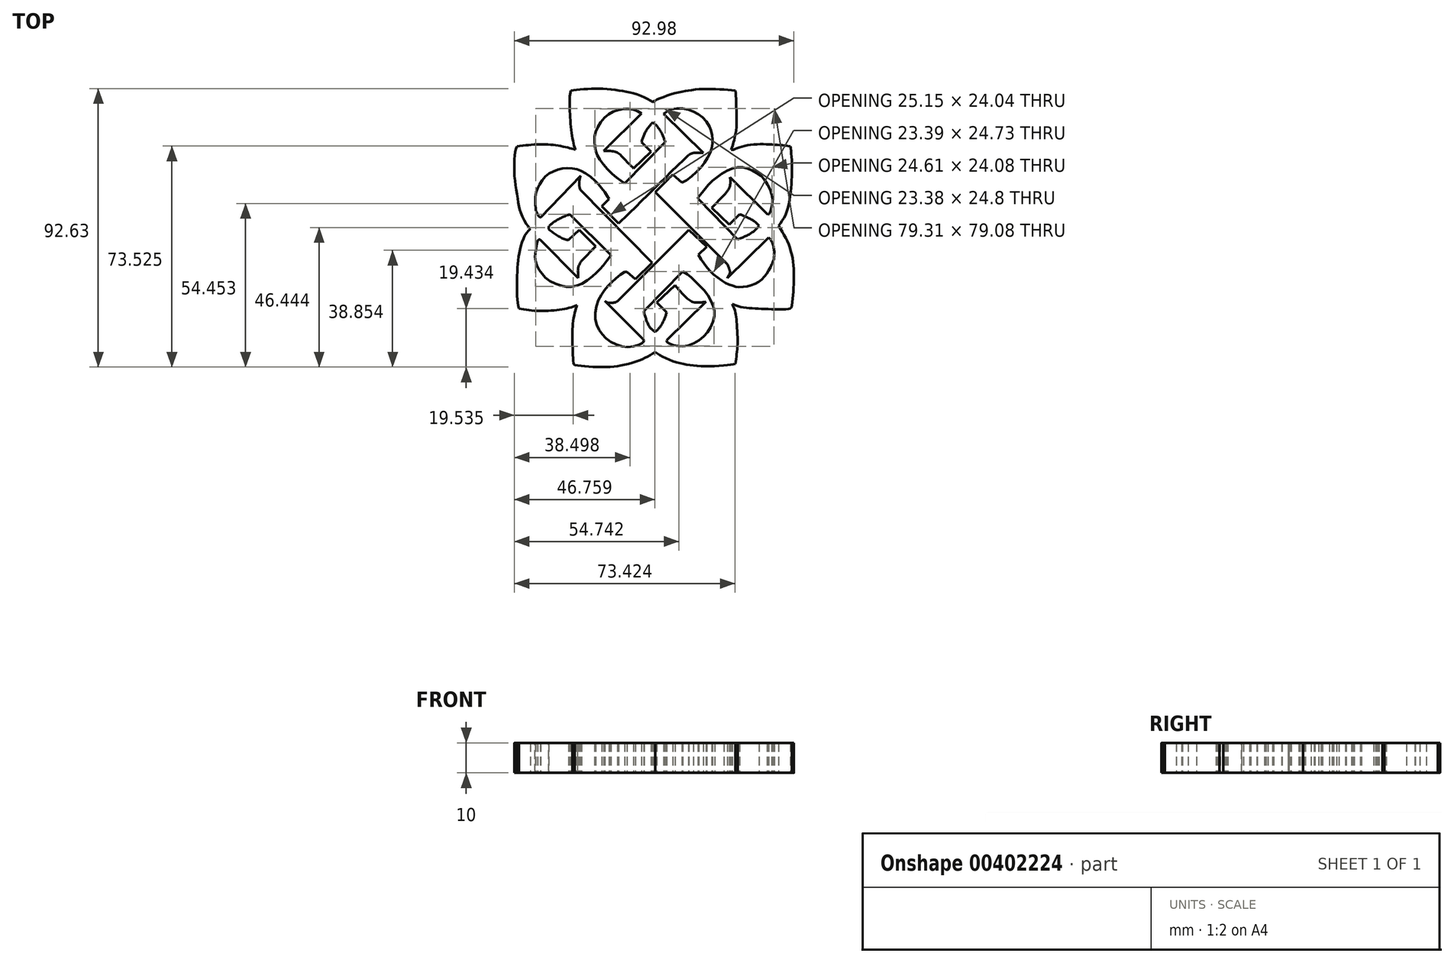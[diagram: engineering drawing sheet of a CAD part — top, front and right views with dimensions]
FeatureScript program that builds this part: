
annotation { "Feature Type Name" : "Feature", "Feature Type Description" : "" }
export const myFeature = defineFeature(function(context is Context, id is Id, definition is map)
    precondition{}
    {
        {
            var Q0;
            Q0=qCreatedBy(makeId("Top.planeOp"),FACE);
            var sketch = newSketch(context, id + "F0", { "sketchPlane" : qUnion([Q0])});
            skFitSpline(sketch, "E0", {"points": [v(25.14, 49.04) * mm, v(30.65, 43.55) * mm], "startDerivative": vector(5.5, -5.49) * mm, "endDerivative": vector(5.5, -5.49) * mm});
            skFitSpline(sketch, "E1", {"points": [v(30.65, 43.55) * mm, v(26, 38.8) * mm], "startDerivative": vector(-4.66, -4.75) * mm, "endDerivative": vector(-4.66, -4.75) * mm});
            skFitSpline(sketch, "E2", {"points": [v(26, 38.8) * mm, v(25.36, 37.84) * mm, v(24.84, 36.64) * mm, v(24.73, 35.05) * mm, v(24.82, 33.01) * mm], "startDerivative": vector(-2.93, -4.28) * mm, "endDerivative": vector(0.35, -7.16) * mm});
            skFitSpline(sketch, "E3", {"points": [v(24.82, 33.01) * mm, v(12.18, 45.71) * mm], "startDerivative": vector(-12.63, 12.7) * mm, "endDerivative": vector(-12.63, 12.7) * mm});
            skFitSpline(sketch, "E4", {"points": [v(12.18, 45.71) * mm, v(11.87, 45.87) * mm, v(11.4, 45.54) * mm], "startDerivative": vector(-0.7, 0.56) * mm, "endDerivative": vector(-0.88, -0.85) * mm});
            skFitSpline(sketch, "E5", {"points": [v(11.4, 45.54) * mm, v(11.08, 44.46) * mm, v(10.68, 42.28) * mm, v(10.47, 40.66) * mm, v(10.64, 38.94) * mm, v(11.02, 37.26) * mm, v(12.18, 35.32) * mm, v(13.55, 33.61) * mm, v(15.9, 31.77) * mm, v(19.27, 30.43) * mm, v(21.46, 30.1) * mm, v(24.16, 30.49) * mm, v(27.14, 31.79) * mm, v(30, 34.01) * mm, v(31.82, 35.74) * mm, v(33.53, 37.63) * mm, v(35.58, 40.39) * mm], "startDerivative": vector(-7.4, -22.6) * mm, "endDerivative": vector(27.9, 39.07) * mm});
            skFitSpline(sketch, "E6", {"points": [v(35.58, 40.39) * mm, v(35.7, 40.73) * mm], "startDerivative": vector(0.11, 0.34) * mm, "endDerivative": vector(0.11, 0.34) * mm});
            skFitSpline(sketch, "E7", {"points": [v(35.7, 40.73) * mm, v(22.01, 54.3) * mm], "startDerivative": vector(-13.68, 13.56) * mm, "endDerivative": vector(-13.68, 13.56) * mm});
            skFitSpline(sketch, "E8", {"points": [v(22.01, 54.3) * mm, v(20.72, 53.8) * mm, v(18.89, 52.95) * mm, v(16.98, 51.84) * mm, v(15.66, 50.83) * mm, v(15.02, 50.13) * mm], "startDerivative": vector(-6.7, -2.48) * mm, "endDerivative": vector(-3.68, -4.51) * mm});
            skFitSpline(sketch, "E9", {"points": [v(15.02, 50.13) * mm, v(15.02, 49.37) * mm, v(16, 48.49) * mm, v(17.72, 47.27) * mm, v(19.6, 46.26) * mm, v(21.13, 45.71) * mm, v(21.66, 45.71) * mm], "startDerivative": vector(-1.24, -6.24) * mm, "endDerivative": vector(4.43, 0.52) * mm});
            skFitSpline(sketch, "E10", {"points": [v(21.66, 45.71) * mm, v(25.14, 49.04) * mm], "startDerivative": vector(3.48, 3.33) * mm, "endDerivative": vector(3.48, 3.33) * mm});
            skFitSpline(sketch, "E11", {"points": [v(12.31, 53.22) * mm, v(11.64, 53.66) * mm, v(11.22, 54.54) * mm, v(10.7, 55.71) * mm], "startDerivative": vector(-2.5, 1.24) * mm, "endDerivative": vector(-1.5, 3.16) * mm});
            skFitSpline(sketch, "E12", {"points": [v(10.7, 55.71) * mm, v(10.7, 60.78) * mm, v(11.4, 63) * mm, v(12.81, 65.5) * mm, v(14.78, 67.61) * mm, v(17.68, 68.96) * mm, v(20.37, 69.6) * mm, v(23.64, 69.38) * mm, v(25.96, 68.59) * mm, v(29.66, 66.11) * mm, v(31.96, 63.76) * mm, v(34.08, 61.07) * mm, v(35.11, 59.3) * mm], "startDerivative": vector(-2.5, 53.11) * mm, "endDerivative": vector(13.02, -25.08) * mm});
            skFitSpline(sketch, "E13", {"points": [v(35.11, 59.3) * mm, v(32.7, 56.92) * mm], "startDerivative": vector(-2.41, -2.37) * mm, "endDerivative": vector(-2.41, -2.37) * mm});
            skFitSpline(sketch, "E14", {"points": [v(32.7, 56.92) * mm, v(38.27, 51.23) * mm], "startDerivative": vector(5.57, -5.69) * mm, "endDerivative": vector(5.57, -5.69) * mm});
            skFitSpline(sketch, "E15", {"points": [v(38.27, 51.23) * mm, v(61.5, 73.93) * mm], "startDerivative": vector(24.3, 23.14) * mm, "endDerivative": vector(24.3, 23.14) * mm});
            skFitSpline(sketch, "E16", {"points": [v(61.5, 73.93) * mm, v(62.34, 74.43) * mm, v(63.17, 74.69) * mm], "startDerivative": vector(1.64, 1.06) * mm, "endDerivative": vector(1.73, 0.44) * mm});
            skFitSpline(sketch, "E17", {"points": [v(63.17, 74.69) * mm, v(66.49, 74.69) * mm], "startDerivative": vector(3.32, 0) * mm, "endDerivative": vector(3.32, 0) * mm});
            skFitSpline(sketch, "E18", {"points": [v(66.49, 74.69) * mm, v(53.29, 87.73) * mm], "startDerivative": vector(-13.2, 13.04) * mm, "endDerivative": vector(-13.2, 13.04) * mm});
            skFitSpline(sketch, "E19", {"points": [v(53.29, 87.73) * mm, v(54.47, 88.62) * mm, v(55.94, 89.26) * mm, v(58.34, 89.41) * mm, v(60.98, 89.22) * mm, v(63.17, 88.39) * mm, v(65.18, 87.28) * mm, v(66.84, 85.95) * mm, v(68.4, 83.69) * mm, v(68.97, 82.34) * mm, v(69.43, 80.48) * mm, v(69.49, 79.36) * mm, v(69.49, 78.04) * mm, v(69.3, 76.26) * mm, v(68.62, 74.49) * mm, v(67.25, 72.07) * mm, v(66.09, 70.37) * mm, v(63.7, 67.91) * mm, v(61.06, 65.73) * mm, v(59.36, 64.86) * mm], "startDerivative": vector(25.95, 21.12) * mm, "endDerivative": vector(-32.62, -14.19) * mm});
            skFitSpline(sketch, "E20", {"points": [v(59.36, 64.86) * mm, v(56.29, 67.53) * mm], "startDerivative": vector(-3.07, 2.67) * mm, "endDerivative": vector(-3.07, 2.67) * mm});
            skFitSpline(sketch, "E21", {"points": [v(56.29, 67.53) * mm, v(50.5, 61.67) * mm], "startDerivative": vector(-5.59, -5.68) * mm, "endDerivative": vector(-5.59, -5.68) * mm});
            skFitSpline(sketch, "E22", {"points": [v(50.5, 61.67) * mm, v(74.45, 37.61) * mm], "startDerivative": vector(23.95, -24.05) * mm, "endDerivative": vector(23.95, -24.05) * mm});
            skFitSpline(sketch, "E23", {"points": [v(74.45, 37.61) * mm, v(74.95, 36.44) * mm, v(75.25, 35.48) * mm, v(75.24, 34.6) * mm, v(74.69, 33.49) * mm, v(74.45, 33.05) * mm], "startDerivative": vector(2.3, -5.17) * mm, "endDerivative": vector(-1.4, -2.62) * mm});
            skFitSpline(sketch, "E24", {"points": [v(74.45, 33.05) * mm, v(87.78, 46.14) * mm], "startDerivative": vector(13.34, 13.08) * mm, "endDerivative": vector(13.34, 13.08) * mm});
            skFitSpline(sketch, "E25", {"points": [v(87.78, 46.14) * mm, v(88.2, 46.52) * mm], "startDerivative": vector(0.41, 0.38) * mm, "endDerivative": vector(0.41, 0.38) * mm});
            skFitSpline(sketch, "E26", {"points": [v(88.2, 46.52) * mm, v(89.14, 45.28) * mm, v(89.63, 43.97) * mm, v(89.97, 42.62) * mm, v(90, 41.19) * mm, v(89.98, 39.58) * mm, v(89.77, 38.8) * mm, v(89.16, 37.61) * mm], "startDerivative": vector(6.84, -7.84) * mm, "endDerivative": vector(-5.3, -9.98) * mm});
            skFitSpline(sketch, "E27", {"points": [v(89.16, 37.61) * mm, v(88.64, 36.4) * mm, v(87.78, 34.91) * mm, v(86.72, 33.48) * mm, v(85.38, 32.15) * mm, v(83.67, 31.12) * mm, v(81.57, 30.46) * mm, v(79.56, 30.08) * mm, v(77.52, 30.08) * mm, v(76.76, 30.4) * mm, v(74.89, 30.9) * mm, v(73.26, 31.77) * mm, v(70.76, 33.48) * mm, v(68.58, 35.56) * mm, v(66.6, 37.9) * mm, v(64.8, 40.78) * mm], "startDerivative": vector(-8.82, -22.5) * mm, "endDerivative": vector(-20.37, 34.98) * mm});
            skFitSpline(sketch, "E28", {"points": [v(64.8, 40.78) * mm, v(67.6, 43.41) * mm], "startDerivative": vector(2.8, 2.63) * mm, "endDerivative": vector(2.8, 2.63) * mm});
            skFitSpline(sketch, "E29", {"points": [v(67.6, 43.41) * mm, v(61.64, 49.1) * mm], "startDerivative": vector(-5.95, 5.69) * mm, "endDerivative": vector(-5.95, 5.69) * mm});
            skFitSpline(sketch, "E30", {"points": [v(61.64, 49.1) * mm, v(37.82, 25.36) * mm], "startDerivative": vector(-23.82, -23.74) * mm, "endDerivative": vector(-23.82, -23.74) * mm});
            skFitSpline(sketch, "E31", {"points": [v(37.82, 25.36) * mm, v(37.15, 24.97) * mm, v(35.4, 24.78) * mm, v(34.37, 24.97) * mm, v(33.48, 25.62) * mm], "startDerivative": vector(-2.6, -2.09) * mm, "endDerivative": vector(-2.88, 3.27) * mm});
            skFitSpline(sketch, "E32", {"points": [v(33.48, 25.62) * mm, v(46.7, 12.3) * mm], "startDerivative": vector(13.23, -13.31) * mm, "endDerivative": vector(13.23, -13.31) * mm});
            skFitSpline(sketch, "E33", {"points": [v(46.7, 12.3) * mm, v(46.12, 11.42) * mm, v(43.3, 10.3) * mm, v(39.34, 10.32) * mm, v(34.88, 12.3) * mm, v(32.37, 15) * mm, v(30.74, 18.2) * mm, v(30.78, 23.4) * mm, v(32.72, 27.8) * mm, v(34.97, 30.76) * mm, v(37.93, 33.45) * mm, v(40.5, 35.17) * mm, v(41.01, 35.13) * mm], "startDerivative": vector(-8.2, -18.96) * mm, "endDerivative": vector(12.87, -4.69) * mm});
            skFitSpline(sketch, "E34", {"points": [v(41.01, 35.13) * mm, v(43.8, 32.67) * mm], "startDerivative": vector(2.78, -2.46) * mm, "endDerivative": vector(2.78, -2.46) * mm});
            skFitSpline(sketch, "E35", {"points": [v(43.8, 32.67) * mm, v(49.4, 38.11) * mm], "startDerivative": vector(5.6, 5.45) * mm, "endDerivative": vector(5.6, 5.45) * mm});
            skFitSpline(sketch, "E36", {"points": [v(49.4, 38.11) * mm, v(25.55, 62.46) * mm], "startDerivative": vector(-23.85, 24.34) * mm, "endDerivative": vector(-23.85, 24.34) * mm});
            skFitSpline(sketch, "E37", {"points": [v(25.55, 62.46) * mm, v(25.17, 63.93) * mm, v(25.32, 65.98) * mm, v(25.62, 67.08) * mm], "startDerivative": vector(-1.47, 4.14) * mm, "endDerivative": vector(1.1, 3.45) * mm});
            skFitSpline(sketch, "E38", {"points": [v(25.62, 67.08) * mm, v(12.31, 53.22) * mm], "startDerivative": vector(-13.31, -13.87) * mm, "endDerivative": vector(-13.31, -13.87) * mm});
            skFitSpline(sketch, "E39", {"points": [v(49.7, 84.86) * mm, v(51.82, 82.58) * mm, v(53.18, 79.87) * mm, v(53.78, 78.24) * mm], "startDerivative": vector(6.22, -5.76) * mm, "endDerivative": vector(1.94, -5.54) * mm});
            skFitSpline(sketch, "E40", {"points": [v(53.78, 78.24) * mm, v(40.32, 64.55) * mm], "startDerivative": vector(-13.46, -13.7) * mm, "endDerivative": vector(-13.46, -13.7) * mm});
            skFitSpline(sketch, "E41", {"points": [v(40.32, 64.55) * mm, v(37.26, 66.71) * mm, v(33.13, 70.93) * mm, v(30.85, 74.68) * mm, v(30.27, 77.58) * mm, v(30.5, 81.1) * mm, v(32.35, 84.96) * mm, v(35.56, 87.94) * mm, v(39.5, 89.25) * mm, v(43.26, 89.1) * mm, v(45.85, 87.78) * mm], "startDerivative": vector(-30.25, 19.46) * mm, "endDerivative": vector(28.26, -18.1) * mm});
            skFitSpline(sketch, "E42", {"points": [v(45.85, 87.78) * mm, v(33.35, 75.33) * mm], "startDerivative": vector(-12.5, -12.46) * mm, "endDerivative": vector(-12.5, -12.46) * mm});
            skFitSpline(sketch, "E43", {"points": [v(33.35, 75.33) * mm, v(36.47, 75.22) * mm, v(38.43, 74.4) * mm, v(40.32, 72.48) * mm, v(43.24, 69.52) * mm], "startDerivative": vector(12.9, 0.35) * mm, "endDerivative": vector(10.5, -10.32) * mm});
            skFitSpline(sketch, "E44", {"points": [v(43.24, 69.52) * mm, v(49.02, 75.08) * mm], "startDerivative": vector(5.79, 5.56) * mm, "endDerivative": vector(5.79, 5.56) * mm});
            skFitSpline(sketch, "E45", {"points": [v(49.02, 75.08) * mm, v(45.85, 78.24) * mm], "startDerivative": vector(-3.18, 3.16) * mm, "endDerivative": vector(-3.18, 3.16) * mm});
            skFitSpline(sketch, "E46", {"points": [v(45.85, 78.24) * mm, v(46.46, 80.06) * mm, v(47.62, 82.38) * mm, v(49.29, 84.45) * mm, v(49.7, 84.86) * mm], "startDerivative": vector(2.19, 6.94) * mm, "endDerivative": vector(2.42, 2.27) * mm});
            skFitSpline(sketch, "E47", {"points": [v(84.95, 50.48) * mm, v(83.34, 48.7) * mm, v(80.36, 46.93) * mm, v(77.84, 45.83) * mm], "startDerivative": vector(-4.56, -5.96) * mm, "endDerivative": vector(-7.4, -3.04) * mm});
            skFitSpline(sketch, "E48", {"points": [v(77.84, 45.83) * mm, v(64.9, 59.25) * mm], "startDerivative": vector(-12.94, 13.42) * mm, "endDerivative": vector(-12.94, 13.42) * mm});
            skFitSpline(sketch, "E49", {"points": [v(64.9, 59.25) * mm, v(64.77, 59.46) * mm, v(64.71, 59.66) * mm, v(64.74, 59.89) * mm, v(64.9, 60.1) * mm], "startDerivative": vector(-0.57, 0.8) * mm, "endDerivative": vector(0.72, 0.77) * mm});
            skFitSpline(sketch, "E50", {"points": [v(64.9, 60.1) * mm, v(68.82, 64.78) * mm, v(71.62, 67.09) * mm, v(75.13, 69.2) * mm, v(78.44, 69.92) * mm, v(80.85, 69.56) * mm, v(83.84, 68.26) * mm, v(86.15, 66.52) * mm, v(88.12, 63.62) * mm, v(89.28, 60.67) * mm, v(89.47, 58.54) * mm, v(89.24, 56.76) * mm, v(88.55, 54.64) * mm, v(88.04, 54.13) * mm, v(87.7, 54.4) * mm], "startDerivative": vector(37.33, 47.72) * mm, "endDerivative": vector(-11.48, 13.7) * mm});
            skFitSpline(sketch, "E51", {"points": [v(87.7, 54.4) * mm, v(75.38, 66.6) * mm], "startDerivative": vector(-12.31, 12.2) * mm, "endDerivative": vector(-12.31, 12.2) * mm});
            skFitSpline(sketch, "E52", {"points": [v(75.38, 66.6) * mm, v(75.38, 64.05) * mm, v(74.9, 62.62) * mm, v(73.35, 60.68) * mm], "startDerivative": vector(0.33, -7.61) * mm, "endDerivative": vector(-5.02, -5.62) * mm});
            skFitSpline(sketch, "E53", {"points": [v(73.35, 60.68) * mm, v(69.22, 56.49) * mm], "startDerivative": vector(-4.13, -4.2) * mm, "endDerivative": vector(-4.13, -4.2) * mm});
            skFitSpline(sketch, "E54", {"points": [v(69.22, 56.49) * mm, v(75.04, 50.86) * mm], "startDerivative": vector(5.82, -5.62) * mm, "endDerivative": vector(5.82, -5.62) * mm});
            skFitSpline(sketch, "E55", {"points": [v(75.04, 50.86) * mm, v(78.52, 54.27) * mm], "startDerivative": vector(3.48, 3.41) * mm, "endDerivative": vector(3.48, 3.41) * mm});
            skFitSpline(sketch, "E56", {"points": [v(78.52, 54.27) * mm, v(80.36, 53.53) * mm, v(83.34, 51.97) * mm, v(84.95, 50.48) * mm], "startDerivative": vector(5.65, -2.18) * mm, "endDerivative": vector(4.43, -4.8) * mm});
            skFitSpline(sketch, "E57", {"points": [v(50.4, 15.13) * mm, v(48.72, 16.62) * mm, v(47.45, 19.22) * mm, v(46.63, 21.95) * mm], "startDerivative": vector(-5.89, 4.24) * mm, "endDerivative": vector(-2.14, 7.84) * mm});
            skFitSpline(sketch, "E58", {"points": [v(46.63, 21.95) * mm, v(59.62, 35.22) * mm], "startDerivative": vector(12.99, 13.27) * mm, "endDerivative": vector(12.99, 13.27) * mm});
            skFitSpline(sketch, "E59", {"points": [v(59.62, 35.22) * mm, v(62.2, 33.48) * mm, v(64.9, 30.86) * mm, v(67.53, 27.96) * mm, v(69.52, 24.14) * mm, v(70.2, 21.43) * mm, v(69.5, 17.96) * mm, v(67.66, 14.73) * mm, v(64.9, 12.24) * mm, v(61.05, 10.52) * mm, v(58.34, 10.47) * mm, v(56.15, 10.88) * mm, v(54.87, 11.45) * mm, v(54.27, 11.8) * mm, v(54.27, 12.3) * mm], "startDerivative": vector(34.07, -20.66) * mm, "endDerivative": vector(3.69, 17.86) * mm});
            skFitSpline(sketch, "E60", {"points": [v(54.27, 12.3) * mm, v(67.28, 25.23) * mm], "startDerivative": vector(13.01, 12.93) * mm, "endDerivative": vector(13.01, 12.93) * mm});
            skFitSpline(sketch, "E61", {"points": [v(67.28, 25.23) * mm, v(65.73, 24.93) * mm, v(65.34, 24.93) * mm, v(63.56, 24.93) * mm, v(61.9, 25.68) * mm, v(60.59, 26.75) * mm, v(57, 30.7) * mm], "startDerivative": vector(-12.17, -2.7) * mm, "endDerivative": vector(-14.29, 16.4) * mm});
            skFitSpline(sketch, "E62", {"points": [v(57, 30.7) * mm, v(50.92, 24.87) * mm], "startDerivative": vector(-6.07, -5.84) * mm, "endDerivative": vector(-6.07, -5.84) * mm});
            skFitSpline(sketch, "E63", {"points": [v(50.92, 24.87) * mm, v(54.27, 21.58) * mm], "startDerivative": vector(3.35, -3.29) * mm, "endDerivative": vector(3.35, -3.29) * mm});
            skFitSpline(sketch, "E64", {"points": [v(54.27, 21.58) * mm, v(53.38, 19.22) * mm, v(51.93, 16.62) * mm, v(50.4, 15.13) * mm], "startDerivative": vector(-2.4, -6.9) * mm, "endDerivative": vector(-5.12, -4.32) * mm});
            skFitSpline(sketch, "E65", {"points": [v(50.4, 8.38) * mm, v(53.09, 6.81) * mm, v(57.87, 4.93) * mm, v(62.03, 4.1) * mm, v(67.28, 3.7) * mm, v(74.44, 4.07) * mm, v(77.17, 4.5) * mm], "startDerivative": vector(17.48, -11.16) * mm, "endDerivative": vector(17.9, 3.47) * mm});
            skFitSpline(sketch, "E66", {"points": [v(77.17, 4.5) * mm, v(77.57, 7.9) * mm, v(77.84, 12.3) * mm, v(77.54, 18.46) * mm, v(77.17, 21.43) * mm, v(76.11, 24.39) * mm], "startDerivative": vector(2.26, 18) * mm, "endDerivative": vector(-6.92, 16.97) * mm});
            skFitSpline(sketch, "E67", {"points": [v(76.11, 24.39) * mm, v(78.52, 23.53) * mm, v(82.58, 23) * mm, v(87.8, 22.74) * mm, v(94.24, 22.7) * mm, v(95.68, 23.12) * mm, v(95.9, 23.9) * mm], "startDerivative": vector(14.71, -6.3) * mm, "endDerivative": vector(0.96, 10.33) * mm});
            skFitSpline(sketch, "E68", {"points": [v(95.9, 23.9) * mm, v(96.41, 29.08) * mm, v(96.54, 35.22) * mm, v(95.9, 40.71) * mm, v(94.15, 45.83) * mm, v(91.45, 50.48) * mm], "startDerivative": vector(2.97, 25.96) * mm, "endDerivative": vector(-14.66, 23.01) * mm});
            skFitSpline(sketch, "E69", {"points": [v(91.45, 50.48) * mm, v(93.12, 52.85) * mm, v(94.63, 56.49) * mm, v(95.52, 62) * mm, v(95.9, 66.6) * mm, v(95.9, 72.04) * mm, v(95.64, 75.21) * mm, v(95.41, 76.92) * mm], "startDerivative": vector(13.79, 18) * mm, "endDerivative": vector(-2.29, 16.73) * mm});
            skFitSpline(sketch, "E70", {"points": [v(95.41, 76.92) * mm, v(91.14, 77.36) * mm, v(85.9, 77.58) * mm, v(79.63, 76.92) * mm, v(76.53, 75.79) * mm, v(75.78, 75.75) * mm], "startDerivative": vector(-19.4, 2.16) * mm, "endDerivative": vector(-7.17, 0.66) * mm});
            skFitSpline(sketch, "E71", {"points": [v(75.78, 75.75) * mm, v(76.37, 77.8) * mm, v(76.87, 79.67) * mm, v(77.47, 83.52) * mm, v(77.47, 87.57) * mm, v(77.38, 91.72) * mm, v(77.17, 95.39) * mm], "startDerivative": vector(4.48, 15.66) * mm, "endDerivative": vector(-1.39, 20.25) * mm});
            skFitSpline(sketch, "E72", {"points": [v(77.17, 95.39) * mm, v(73.59, 95.75) * mm, v(69.68, 95.92) * mm, v(65.59, 95.9) * mm, v(62.2, 95.56) * mm, v(59.85, 95.19) * mm, v(56.45, 94.42) * mm, v(53.44, 93.36) * mm, v(50.92, 92.35) * mm, v(49.7, 91.55) * mm], "startDerivative": vector(-29.53, 3.37) * mm, "endDerivative": vector(-14.1, -10.68) * mm});
            skFitSpline(sketch, "E73", {"points": [v(49.7, 91.55) * mm, v(46.92, 93.15) * mm, v(42.76, 94.62) * mm, v(38.68, 95.39) * mm, v(33.99, 96) * mm, v(29.5, 96) * mm, v(25.19, 95.8) * mm, v(22.34, 95.39) * mm], "startDerivative": vector(-20.25, 12.93) * mm, "endDerivative": vector(-22.16, -3.85) * mm});
            skFitSpline(sketch, "E74", {"points": [v(22.34, 95.39) * mm, v(21.98, 93.2) * mm, v(22.02, 89.57) * mm, v(22.34, 83.81) * mm, v(23.06, 78.77) * mm, v(23.85, 75.75) * mm], "startDerivative": vector(-2.95, -13.72) * mm, "endDerivative": vector(4.55, -15.72) * mm});
            skFitSpline(sketch, "E75", {"points": [v(23.85, 75.75) * mm, v(21.61, 76.39) * mm, v(18.23, 77.1) * mm, v(14.2, 77.52) * mm, v(9.5, 77.4) * mm, v(4.43, 76.92) * mm], "startDerivative": vector(-13.75, 4.1) * mm, "endDerivative": vector(-23.14, -2.31) * mm});
            skFitSpline(sketch, "E76", {"points": [v(4.43, 76.92) * mm, v(3.76, 74.64) * mm, v(3.61, 71.13) * mm, v(3.67, 66.6) * mm, v(4.43, 61.52) * mm, v(5, 57.31) * mm, v(5.93, 54.4) * mm, v(7.65, 50.86) * mm, v(8.57, 49.86) * mm, v(8.9, 49.5) * mm], "startDerivative": vector(-4.34, -22.03) * mm, "endDerivative": vector(6.6, -7.37) * mm});
            skFitSpline(sketch, "E77", {"points": [v(8.9, 49.5) * mm, v(7.23, 47.46) * mm, v(5.77, 43.64) * mm, v(4.92, 39.6) * mm, v(4.57, 35.22) * mm, v(4.43, 30.08) * mm, v(4.65, 25.68) * mm, v(5.05, 22.93) * mm], "startDerivative": vector(-15.02, -15.35) * mm, "endDerivative": vector(2.9, -21.56) * mm});
            skFitSpline(sketch, "E78", {"points": [v(5.05, 22.93) * mm, v(10.2, 22.17) * mm, v(16.08, 22.26) * mm, v(21.14, 22.93) * mm, v(24.39, 24.08) * mm], "startDerivative": vector(19.52, -3.66) * mm, "endDerivative": vector(14.5, 6.1) * mm});
            skFitSpline(sketch, "E79", {"points": [v(24.39, 24.08) * mm, v(23.9, 22.3) * mm, v(23.14, 18.53) * mm, v(22.92, 14.26) * mm, v(23.01, 8.7) * mm, v(23.37, 4.52) * mm, v(23.59, 4.08) * mm], "startDerivative": vector(-3.57, -12.36) * mm, "endDerivative": vector(3.48, -4.68) * mm});
            skFitSpline(sketch, "E80", {"points": [v(23.59, 4.08) * mm, v(28.2, 3.58) * mm, v(34.81, 3.47) * mm, v(39.52, 4.08) * mm, v(44.64, 5.43) * mm, v(47.87, 6.9) * mm, v(50.4, 8.38) * mm], "startDerivative": vector(25.65, -3.37) * mm, "endDerivative": vector(18.68, 11.11) * mm});
            skSolve(sketch);
        }
        {
            var Q0;
            Q0 = qSketchRegion(id + "F0", true);
            extrude(context, id + "F1", {"entities" : qUnion([Q0]), "depth" : 10 * mm, "offsetDistance" : 25 * mm});
        }
    });
